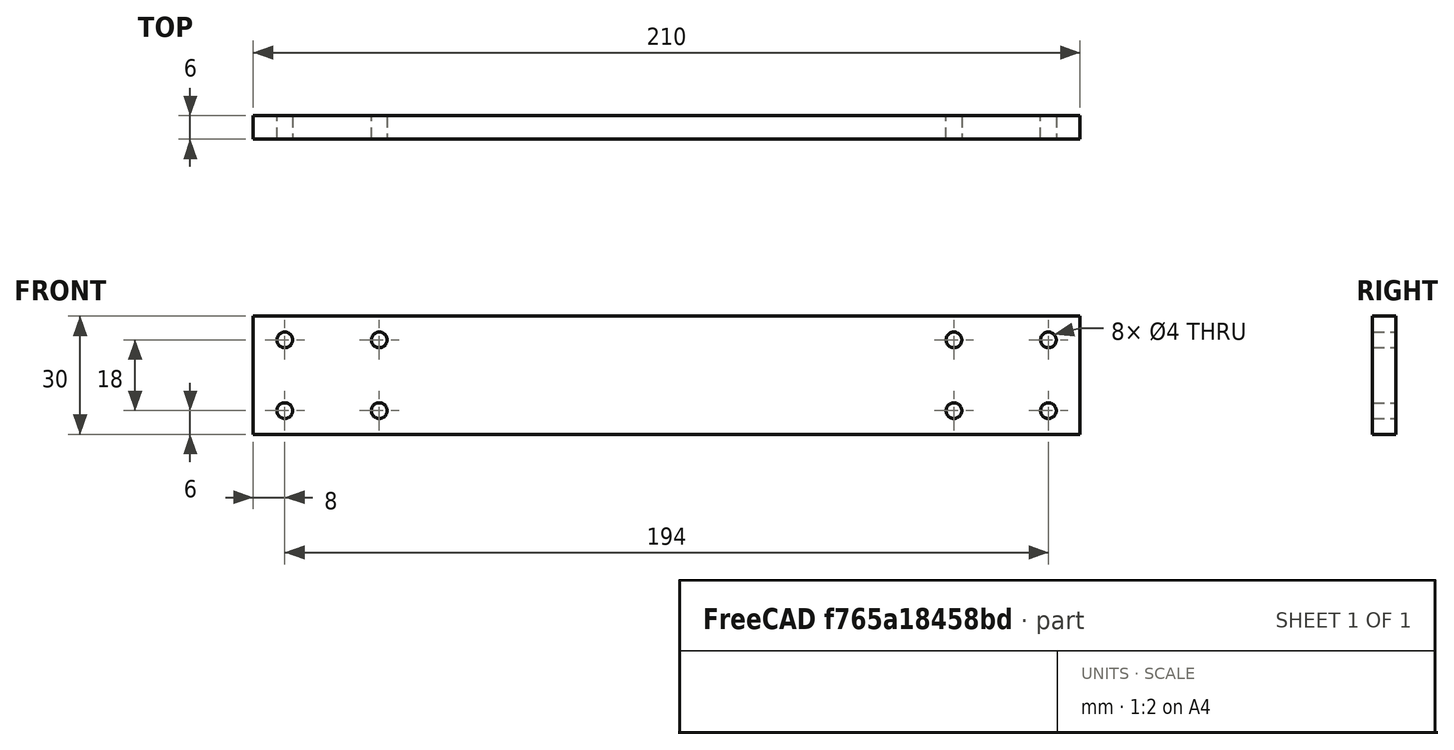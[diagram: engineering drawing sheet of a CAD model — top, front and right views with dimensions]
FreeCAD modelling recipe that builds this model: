
FCSTD DOCUMENT  (FreeCAD 0.18R4 (GitTag))
Label: carro
License: All rights reserved
LicenseURL: http://en.wikipedia.org/wiki/All_rights_reserved
objects: Sketcher::SketchObject×1, PartDesign::Pad×1, PartDesign::Body×1
note: 4 computed .brp shape members not serialized (recipe doc carries the construction recipe); baked Part::Feature solids carry a one-line shape summary decoded from their .brp

FEATURE [Sketcher::SketchObject] Sketch
  MapMode = 5
  Placement = pos=(0,0,0) rot=(1,0,0;1.5708rad)
  Support = -> [XZ_Plane]
  sketch-geometry (12):
    g0: LineSegment StartX=0 StartY=0 StartZ=0 EndX=210 EndY=0 EndZ=0
    g1: LineSegment StartX=210 StartY=0 StartZ=0 EndX=210 EndY=30 EndZ=0
    g2: LineSegment StartX=210 StartY=30 StartZ=0 EndX=0 EndY=30 EndZ=0
    g3: LineSegment StartX=0 StartY=30 StartZ=0 EndX=0 EndY=0 EndZ=0
    g4: Circle CenterX=8 CenterY=24 CenterZ=0 NormalX=0 NormalY=0 NormalZ=1 AngleXU=0 Radius=2
    g5: Circle CenterX=32 CenterY=24 CenterZ=0 NormalX=0 NormalY=0 NormalZ=1 AngleXU=0 Radius=2
    g6: Circle CenterX=8 CenterY=6 CenterZ=0 NormalX=0 NormalY=0 NormalZ=1 AngleXU=0 Radius=2
    g7: Circle CenterX=32 CenterY=6 CenterZ=0 NormalX=0 NormalY=0 NormalZ=1 AngleXU=0 Radius=2
    g8: Circle CenterX=178 CenterY=24 CenterZ=0 NormalX=0 NormalY=0 NormalZ=1 AngleXU=0 Radius=2
    g9: Circle CenterX=202 CenterY=24 CenterZ=0 NormalX=0 NormalY=0 NormalZ=1 AngleXU=0 Radius=2
    g10: Circle CenterX=178 CenterY=6 CenterZ=0 NormalX=0 NormalY=0 NormalZ=1 AngleXU=0 Radius=2
    g11: Circle CenterX=202 CenterY=6 CenterZ=0 NormalX=0 NormalY=0 NormalZ=1 AngleXU=0 Radius=2
  constraints (35):
    c: Coincident(g0,g1)
    c: Coincident(g1,g2)
    c: Coincident(g2,g3)
    c: Coincident(g3,g0)
    c: Horizontal(g0)
    c: Horizontal(g2)
    c: Vertical(g1)
    c: Vertical(g3)
    c: Coincident(g0,g-1)
    c: DistanceX(g0,g0) = 210
    c: DistanceY(g3,g3) = 30
    c: Equal(g4,g5)
    c: Equal(g5,g7)
    c: Equal(g7,g6)
    c: Radius(g5) = 2
    c: DistanceY(g4,g5) = 0
    c: DistanceY(g6,g7) = 0
    c: DistanceX(g5,g7) = 0
    c: DistanceX(g6,g4) = 0
    c: Equal(g8,g9)
    c: Equal(g9,g11)
    c: Equal(g11,g10)
    c: Equal(g5,g9) = 2
    c: DistanceY(g8,g9) = 0
    c: DistanceY(g10,g11) = 0
    c: DistanceX(g9,g11) = 0
    c: DistanceX(g10,g8) = 0
    c: DistanceX(g4,g8) = 170
    c: DistanceX(g4,g5) = 24
    c: DistanceY(g6,g4) = 18
    c: Distance(g6,g3) = 8
    c: Distance(g6,g0) = 6
    c: DistanceX(g8,g9) = 24
    c: DistanceY(g11,g9) = 18
    c: Distance(g11,g0) = 6
FEATURE [PartDesign::Pad] Pad
  Length = 6
  Length2 = 100
  Placement = pos=(0,0,0) rot=(1,0,0;1.5708rad)
  Profile = -> Sketch
  Type = 0
FEATURE [PartDesign::Body] Body
  Group = -> [Sketch,Pad]
  Origin = -> Origin
  Tip = -> Pad
